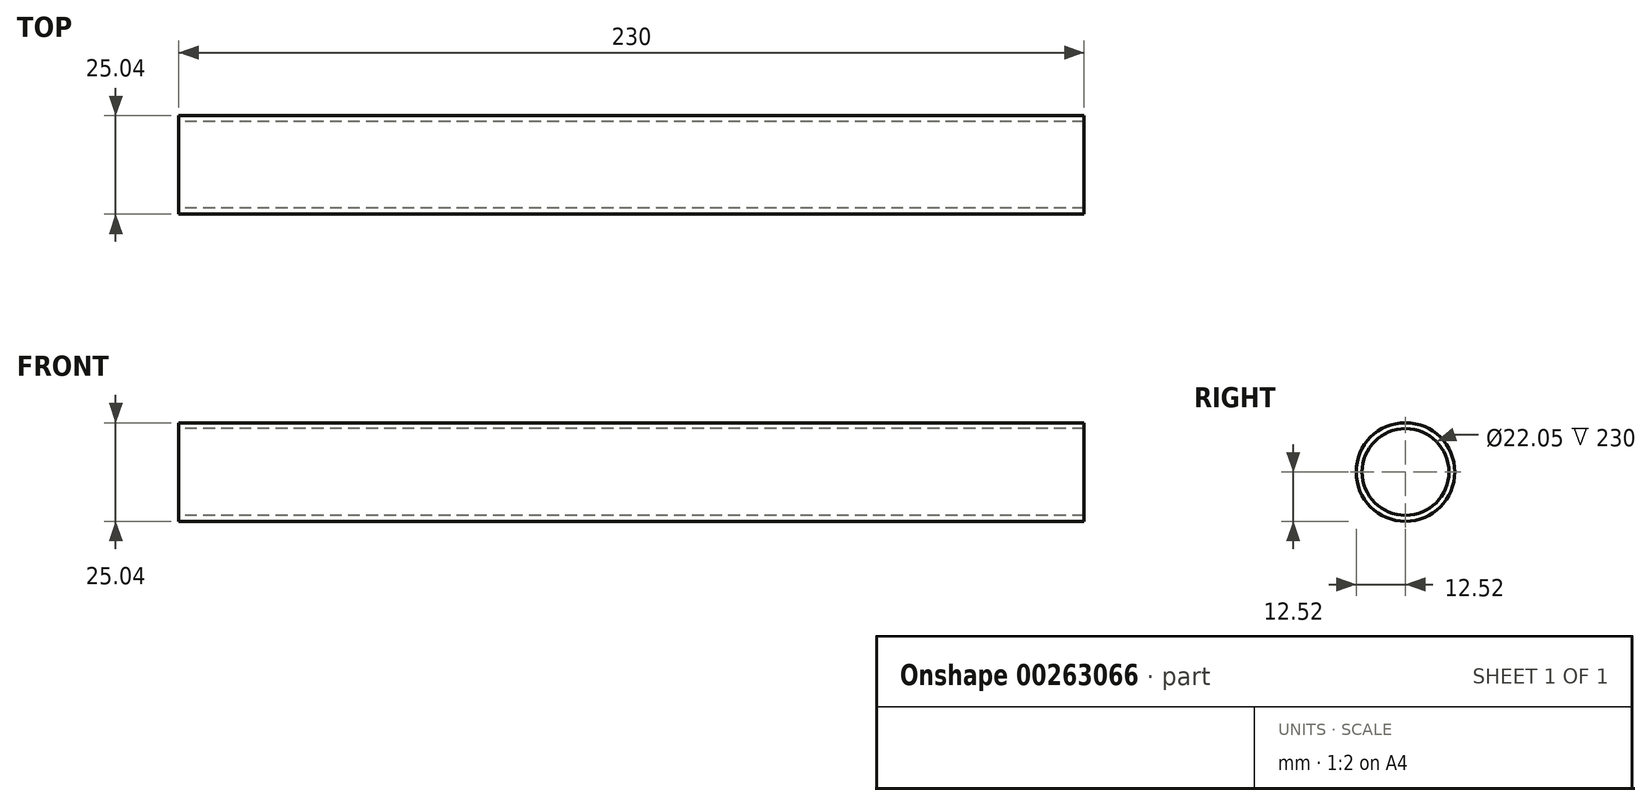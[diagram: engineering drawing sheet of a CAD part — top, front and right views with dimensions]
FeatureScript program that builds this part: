
annotation { "Feature Type Name" : "Feature", "Feature Type Description" : "" }
export const myFeature = defineFeature(function(context is Context, id is Id, definition is map)
    precondition{}
    {
        {
            var Q0;
            Q0=qCreatedBy(makeId("Right.planeOp"),FACE);
            var sketch = newSketch(context, id + "F0", { "sketchPlane" : qUnion([Q0])});
            skCircle(sketch, "E0", {"center": v(0, 0) * mm, "radius": 11.02 * mm});
            skCircle(sketch, "E1", {"center": v(0, 0) * mm, "radius": 12.52 * mm});
            skSolve(sketch);
        }
        {
            var Q0;
            Q0=makeQuery(id+"F0.imprint","IMPRINT",FACE,{"disambiguationData":[TD([[makeQuery(id+"F0.imprint","IMPRINT",EDGE,{"derivedFrom":sQuery(id+"F0.wireOp",EDGE,"E0")}),-1.0]])]});
            extrude(context, id + "F1", {"entities" : qUnion([Q0]), "depth" : 230 * mm});
        }
    });
